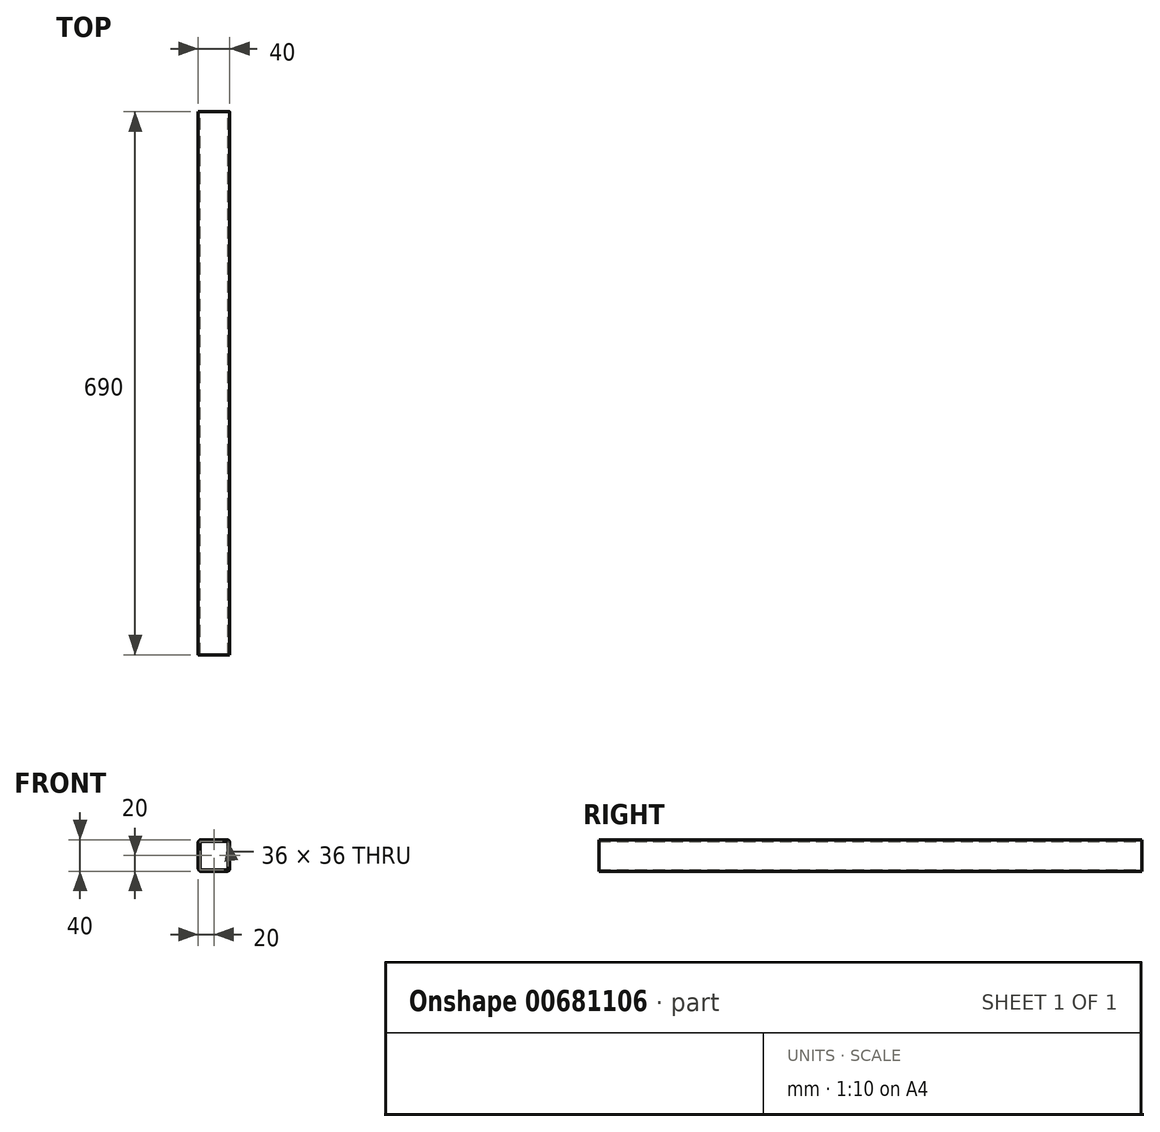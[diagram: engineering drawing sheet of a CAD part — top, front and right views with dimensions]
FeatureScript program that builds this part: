
annotation { "Feature Type Name" : "Feature", "Feature Type Description" : "" }
export const myFeature = defineFeature(function(context is Context, id is Id, definition is map)
    precondition{}
    {
        {
            var Q0;
            Q0=qCreatedBy(makeId("Front.planeOp"),FACE);
            var sketch = newSketch(context, id + "F0", { "sketchPlane" : qUnion([Q0])});
            skLineSegment(sketch, "E0.bottom", {"start": v(18, -18) * mm, "end": v(-18, -18) * mm});
            skLineSegment(sketch, "E0.top", {"start": v(18, 18) * mm, "end": v(-18, 18) * mm});
            skLineSegment(sketch, "E0.left", {"start": v(18, -18) * mm, "end": v(18, 18) * mm});
            skLineSegment(sketch, "E0.right", {"start": v(-18, -18) * mm, "end": v(-18, 18) * mm});
            skPoint(sketch, "E0.middle", {"position": v(0, 0) * mm});
            skLineSegment(sketch, "E1.bottom", {"start": v(16.5, -20) * mm, "end": v(-16.5, -20) * mm});
            skLineSegment(sketch, "E1.top", {"start": v(16.5, 20) * mm, "end": v(-16.5, 20) * mm});
            skLineSegment(sketch, "E1.left", {"start": v(20, -16.5) * mm, "end": v(20, 16.5) * mm});
            skLineSegment(sketch, "E1.right", {"start": v(-20, -16.5) * mm, "end": v(-20, 16.5) * mm});
            skPoint(sketch, "E2.visualSharp", {"position": v(-20, 20) * mm});
            skArc(sketch, "E2.filletArc", {"start": v(-16.5, 20) * mm, "mid": v(-18.97, 18.97) * mm, "end": v(-20, 16.5) * mm});
            skPoint(sketch, "E3.visualSharp", {"position": v(20, 20) * mm});
            skArc(sketch, "E3.filletArc", {"start": v(20, 16.5) * mm, "mid": v(18.97, 18.97) * mm, "end": v(16.5, 20) * mm});
            skPoint(sketch, "E4.visualSharp", {"position": v(20, -20) * mm});
            skArc(sketch, "E4.filletArc", {"start": v(16.5, -20) * mm, "mid": v(18.97, -18.97) * mm, "end": v(20, -16.5) * mm});
            skPoint(sketch, "E5.visualSharp", {"position": v(-20, -20) * mm});
            skArc(sketch, "E5.filletArc", {"start": v(-20, -16.5) * mm, "mid": v(-18.97, -18.97) * mm, "end": v(-16.5, -20) * mm});
            skSolve(sketch);
        }
        {
            var Q0;
            Q0=makeQuery(id+"F0.imprint","IMPRINT",FACE,{"disambiguationData":[TD([[makeQuery(id+"F0.imprint","IMPRINT",EDGE,{"derivedFrom":sQuery(id+"F0.wireOp",EDGE,"E0.bottom")}),1.0]])]});
            extrude(context, id + "F1", {"entities" : qUnion([Q0]), "depth" : 690 * mm, "offsetDistance" : 25 * mm});
        }
    });
